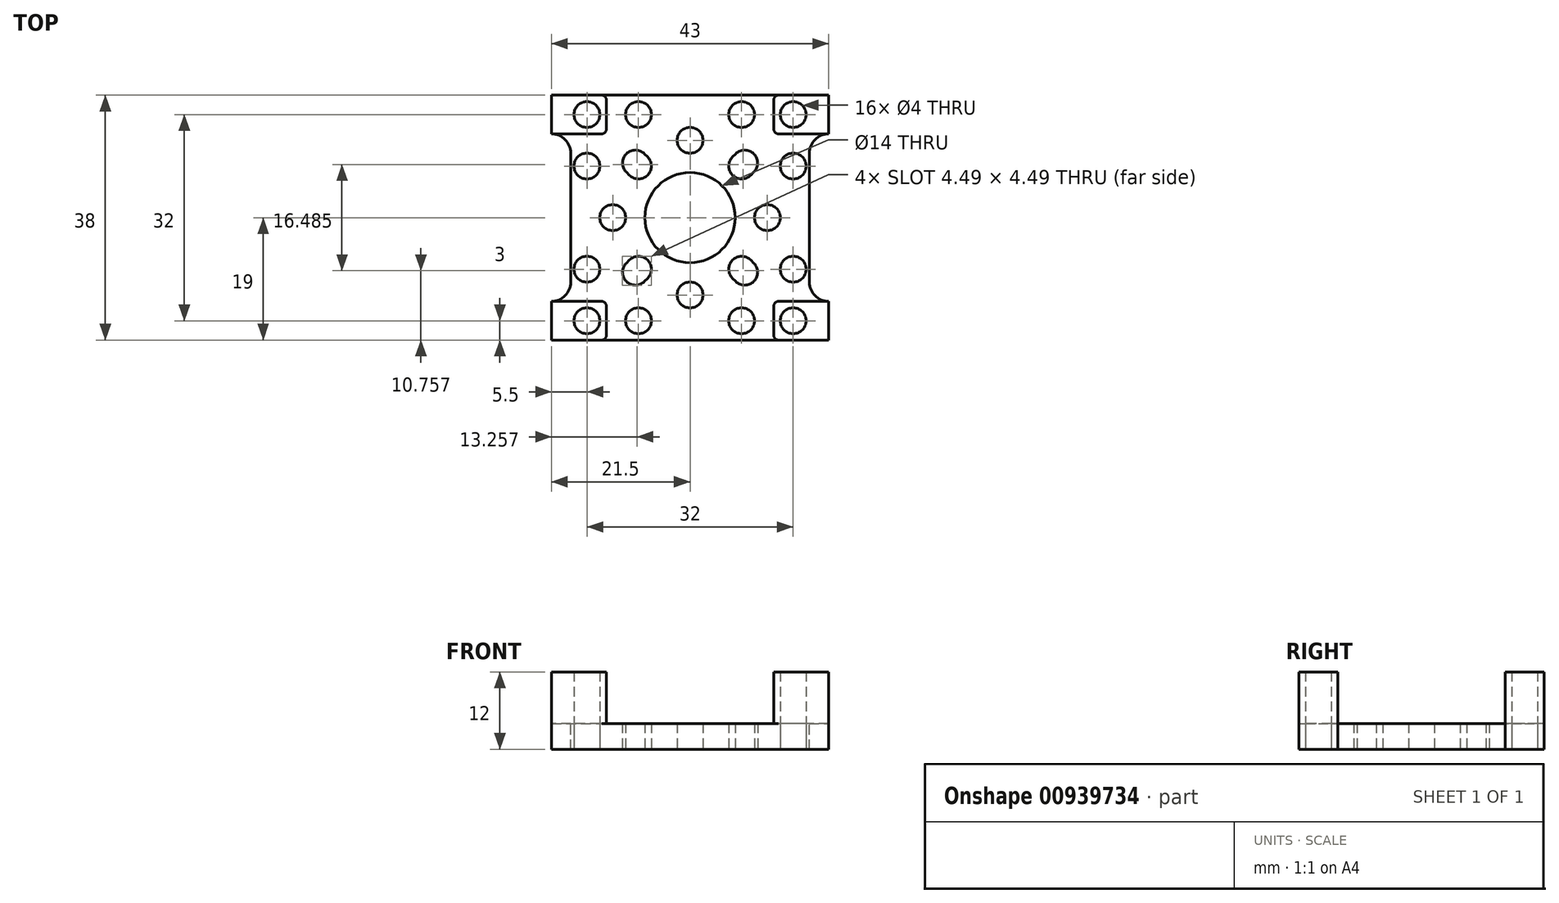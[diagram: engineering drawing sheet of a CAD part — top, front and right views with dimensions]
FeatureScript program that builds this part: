
annotation { "Feature Type Name" : "Feature", "Feature Type Description" : "" }
export const myFeature = defineFeature(function(context is Context, id is Id, definition is map)
    precondition{}
    {
        {
            var Q0;
            Q0=qCreatedBy(makeId("Top.planeOp"),FACE);
            var sketch = newSketch(context, id + "F0", { "sketchPlane" : qUnion([Q0])});
            skCircle(sketch, "E0", {"center": v(0, 0) * mm, "radius": 7 * mm});
            skCircle(sketch, "E1", {"center": v(0, 12) * mm, "radius": 2 * mm});
            skCircle(sketch, "E2", {"center": v(0, -12) * mm, "radius": 2 * mm});
            skCircle(sketch, "E3", {"center": v(12, 0) * mm, "radius": 2 * mm});
            skCircle(sketch, "E4", {"center": v(-12, 0) * mm, "radius": 2 * mm});
            skLineSegment(sketch, "E5", {"start": v(0, 12) * mm, "end": v(0, 0) * mm, "construction": true});
            skLineSegment(sketch, "E6", {"start": v(0, -12) * mm, "end": v(0, 0) * mm, "construction": true});
            skLineSegment(sketch, "E7", {"start": v(12, 0) * mm, "end": v(0, 0) * mm, "construction": true});
            skLineSegment(sketch, "E8", {"start": v(-12, 0) * mm, "end": v(0, 0) * mm, "construction": true});
            skLineSegment(sketch, "E9.bottom", {"start": v(8, 8) * mm, "end": v(-8, 8) * mm, "construction": true});
            skLineSegment(sketch, "E9.top", {"start": v(8, -8) * mm, "end": v(-8, -8) * mm, "construction": true});
            skLineSegment(sketch, "E9.left", {"start": v(8, 8) * mm, "end": v(8, -8) * mm, "construction": true});
            skLineSegment(sketch, "E9.right", {"start": v(-8, 8) * mm, "end": v(-8, -8) * mm, "construction": true});
            skArc(sketch, "E10", {"start": v(6.59, 9.41) * mm, "mid": v(6.59, 6.59) * mm, "end": v(9.41, 6.59) * mm});
            skArc(sketch, "E11", {"start": v(-9.41, 6.59) * mm, "mid": v(-6.59, 6.59) * mm, "end": v(-6.59, 9.41) * mm});
            skArc(sketch, "E12", {"start": v(-6.59, -9.41) * mm, "mid": v(-6.59, -6.59) * mm, "end": v(-9.41, -6.59) * mm});
            skArc(sketch, "E13", {"start": v(9.41, -6.59) * mm, "mid": v(6.59, -6.59) * mm, "end": v(6.59, -9.41) * mm});
            skLineSegment(sketch, "E14", {"start": v(0, 0) * mm, "end": v(-8.49, 8.49) * mm, "construction": true});
            skArc(sketch, "E15", {"start": v(-7.07, 9.9) * mm, "mid": v(-9.9, 9.9) * mm, "end": v(-9.9, 7.07) * mm});
            skLineSegment(sketch, "E16", {"start": v(0, 0) * mm, "end": v(8.49, 8.49) * mm, "construction": true});
            skLineSegment(sketch, "E17", {"start": v(0, 0) * mm, "end": v(8.49, -8.49) * mm, "construction": true});
            skLineSegment(sketch, "E18", {"start": v(0, 0) * mm, "end": v(-8.49, -8.49) * mm, "construction": true});
            skArc(sketch, "E19", {"start": v(7.07, -9.9) * mm, "mid": v(9.9, -9.9) * mm, "end": v(9.9, -7.07) * mm});
            skArc(sketch, "E20", {"start": v(-9.9, -7.07) * mm, "mid": v(-9.9, -9.9) * mm, "end": v(-7.07, -9.9) * mm});
            skLineSegment(sketch, "E21", {"start": v(-6.59, 9.41) * mm, "end": v(-7.07, 9.9) * mm});
            skLineSegment(sketch, "E22", {"start": v(-9.9, 7.07) * mm, "end": v(-9.41, 6.59) * mm});
            skLineSegment(sketch, "E23", {"start": v(9.9, 7.07) * mm, "end": v(9.41, 6.59) * mm});
            skLineSegment(sketch, "E24", {"start": v(7.07, 9.9) * mm, "end": v(6.59, 9.41) * mm});
            skLineSegment(sketch, "E25", {"start": v(9.41, -6.59) * mm, "end": v(9.9, -7.07) * mm});
            skLineSegment(sketch, "E26", {"start": v(6.59, -9.41) * mm, "end": v(7.07, -9.9) * mm});
            skLineSegment(sketch, "E27", {"start": v(-9.41, -6.59) * mm, "end": v(-9.9, -7.07) * mm});
            skLineSegment(sketch, "E28", {"start": v(-6.59, -9.41) * mm, "end": v(-7.07, -9.9) * mm});
            skArc(sketch, "E29.trimOffspring", {"start": v(9.9, 7.07) * mm, "mid": v(9.9, 9.9) * mm, "end": v(7.07, 9.9) * mm});
            skLineSegment(sketch, "E30.bottom", {"start": v(0, 0) * mm, "end": v(16, 0) * mm, "construction": true});
            skLineSegment(sketch, "E30.top", {"start": v(0, 16) * mm, "end": v(16, 16) * mm, "construction": true});
            skLineSegment(sketch, "E30.left", {"start": v(0, 0) * mm, "end": v(0, 16) * mm, "construction": true});
            skLineSegment(sketch, "E30.right", {"start": v(16, 0) * mm, "end": v(16, 16) * mm, "construction": true});
            skCircle(sketch, "E31", {"center": v(16, 16) * mm, "radius": 2 * mm});
            skCircle(sketch, "E32", {"center": v(8, 16) * mm, "radius": 2 * mm});
            skCircle(sketch, "E33", {"center": v(16, 8) * mm, "radius": 2 * mm});
            skPoint(sketch, "E33.perimeterSnap0", {"position": v(16, 8) * mm});
            skCircle(sketch, "E34.1.0", {"center": v(-16, 8) * mm, "radius": 2 * mm});
            skCircle(sketch, "E34.1.1", {"center": v(-16, 16) * mm, "radius": 2 * mm});
            skCircle(sketch, "E34.1.2", {"center": v(-8, 16) * mm, "radius": 2 * mm});
            skCircle(sketch, "E34.2.0", {"center": v(-8, -16) * mm, "radius": 2 * mm});
            skCircle(sketch, "E34.2.1", {"center": v(-16, -16) * mm, "radius": 2 * mm});
            skCircle(sketch, "E34.2.2", {"center": v(-16, -8) * mm, "radius": 2 * mm});
            skCircle(sketch, "E34.3.0", {"center": v(16, -8) * mm, "radius": 2 * mm});
            skCircle(sketch, "E34.3.1", {"center": v(16, -16) * mm, "radius": 2 * mm});
            skCircle(sketch, "E34.3.2", {"center": v(8, -16) * mm, "radius": 2 * mm});
            skLineSegment(sketch, "E35.bottom", {"start": v(21.5, 19) * mm, "end": v(-21.5, 19) * mm});
            skLineSegment(sketch, "E35.top", {"start": v(21.5, -19) * mm, "end": v(-21.5, -19) * mm});
            skLineSegment(sketch, "E35.left", {"start": v(21.5, 19) * mm, "end": v(21.5, -19) * mm});
            skLineSegment(sketch, "E35.right", {"start": v(-21.5, 19) * mm, "end": v(-21.5, -19) * mm});
            skSolve(sketch);
        }
        {
            var Q0;
            Q0=qSketchRegion(id+"F0",true);
            extrude(context, id + "F1", {"entities" : qUnion([Q0]), "depth" : 4 * mm, "offsetDistance" : 25 * mm});
        }
        {
            var Q0;
            Q0=makeQuery(id+"F1.opExtrude","CAP_FACE",FACE,{"disambiguationData":[OSD([sQuery(id+"F0.wireOp",EDGE,"E0"),sQuery(id+"F0.wireOp",EDGE,"E1"),sQuery(id+"F0.wireOp",EDGE,"E2"),sQuery(id+"F0.wireOp",EDGE,"E3"),sQuery(id+"F0.wireOp",EDGE,"E4"),sQuery(id+"F0.wireOp",EDGE,"E10"),sQuery(id+"F0.wireOp",EDGE,"E11"),sQuery(id+"F0.wireOp",EDGE,"E12"),sQuery(id+"F0.wireOp",EDGE,"E13"),sQuery(id+"F0.wireOp",EDGE,"E15"),sQuery(id+"F0.wireOp",EDGE,"E19"),sQuery(id+"F0.wireOp",EDGE,"E20"),sQuery(id+"F0.wireOp",EDGE,"E21"),sQuery(id+"F0.wireOp",EDGE,"E22"),sQuery(id+"F0.wireOp",EDGE,"E23"),sQuery(id+"F0.wireOp",EDGE,"E24"),sQuery(id+"F0.wireOp",EDGE,"E25"),sQuery(id+"F0.wireOp",EDGE,"E26"),sQuery(id+"F0.wireOp",EDGE,"E27"),sQuery(id+"F0.wireOp",EDGE,"E28"),sQuery(id+"F0.wireOp",EDGE,"E29.trimOffspring"),sQuery(id+"F0.wireOp",EDGE,"E31"),sQuery(id+"F0.wireOp",EDGE,"E32"),sQuery(id+"F0.wireOp",EDGE,"E33"),sQuery(id+"F0.wireOp",EDGE,"E34.1.0"),sQuery(id+"F0.wireOp",EDGE,"E34.1.1"),sQuery(id+"F0.wireOp",EDGE,"E34.1.2"),sQuery(id+"F0.wireOp",EDGE,"E34.2.0"),sQuery(id+"F0.wireOp",EDGE,"E34.2.1"),sQuery(id+"F0.wireOp",EDGE,"E34.2.2"),sQuery(id+"F0.wireOp",EDGE,"E34.3.0"),sQuery(id+"F0.wireOp",EDGE,"E34.3.1"),sQuery(id+"F0.wireOp",EDGE,"E34.3.2"),sQuery(id+"F0.wireOp",EDGE,"E35.bottom"),sQuery(id+"F0.wireOp",EDGE,"E35.top"),sQuery(id+"F0.wireOp",EDGE,"E35.left"),sQuery(id+"F0.wireOp",EDGE,"E35.right")])],"isStart":false});
            var sketch = newSketch(context, id + "F2", { "sketchPlane" : qUnion([Q0])});
            skLineSegment(sketch, "E36.0", {"start": v(21.5, 19) * mm, "end": v(-21.5, 19) * mm, "construction": true});
            skLineSegment(sketch, "E37.0", {"start": v(-21.5, 19) * mm, "end": v(-21.5, -19) * mm, "construction": true});
            skLineSegment(sketch, "E38.bottom", {"start": v(-21.5, 19) * mm, "end": v(-13, 19) * mm});
            skLineSegment(sketch, "E38.top", {"start": v(-21.5, 13) * mm, "end": v(-13, 13) * mm});
            skLineSegment(sketch, "E38.left", {"start": v(-21.5, 19) * mm, "end": v(-21.5, 13) * mm});
            skLineSegment(sketch, "E38.right", {"start": v(-13, 19) * mm, "end": v(-13, 13) * mm});
            skLineSegment(sketch, "E39.bottom", {"start": v(21.5, 19) * mm, "end": v(13, 19) * mm});
            skLineSegment(sketch, "E39.top", {"start": v(21.5, 13) * mm, "end": v(13, 13) * mm});
            skLineSegment(sketch, "E39.left", {"start": v(21.5, 19) * mm, "end": v(21.5, 13) * mm});
            skLineSegment(sketch, "E39.right", {"start": v(13, 19) * mm, "end": v(13, 13) * mm});
            skLineSegment(sketch, "E40.1.0", {"start": v(13, -19) * mm, "end": v(13, -13) * mm});
            skLineSegment(sketch, "E40.1.1", {"start": v(-13, -19) * mm, "end": v(-13, -13) * mm});
            skLineSegment(sketch, "E40.1.2", {"start": v(-21.5, -19) * mm, "end": v(21.5, -19) * mm, "construction": true});
            skLineSegment(sketch, "E40.1.3", {"start": v(21.5, -19) * mm, "end": v(21.5, -13) * mm});
            skLineSegment(sketch, "E40.1.4", {"start": v(-21.5, -13) * mm, "end": v(-13, -13) * mm});
            skLineSegment(sketch, "E40.1.5", {"start": v(21.5, -13) * mm, "end": v(13, -13) * mm});
            skLineSegment(sketch, "E40.1.6", {"start": v(-21.5, -19) * mm, "end": v(-21.5, -13) * mm});
            skLineSegment(sketch, "E40.1.7", {"start": v(21.5, -19) * mm, "end": v(13, -19) * mm});
            skLineSegment(sketch, "E40.1.8", {"start": v(-21.5, -19) * mm, "end": v(-13, -19) * mm});
            skPoint(sketch, "E40.center", {"position": v(0, 0) * mm});
            skCircle(sketch, "E41.0", {"center": v(-16, 16) * mm, "radius": 2 * mm});
            skCircle(sketch, "E42.0", {"center": v(16, 16) * mm, "radius": 2 * mm});
            skCircle(sketch, "E43.0", {"center": v(16, -16) * mm, "radius": 2 * mm});
            skCircle(sketch, "E44.0", {"center": v(-16, -16) * mm, "radius": 2 * mm});
            skSolve(sketch);
        }
        {
            var Q0;
            Q0=qSketchRegion(id+"F2",true);
            extrude(context, id + "F3", {"entities" : qUnion([Q0]), "operationType" : NewBodyOperationType.ADD, "depth" : 8 * mm, "offsetDistance" : 25 * mm});
        }
        {
            var Q0;
            Q0=makeQuery(id+"F1.opExtrude","CAP_FACE",FACE,{"disambiguationData":[OSD([sQuery(id+"F0.wireOp",EDGE,"E0"),sQuery(id+"F0.wireOp",EDGE,"E1"),sQuery(id+"F0.wireOp",EDGE,"E2"),sQuery(id+"F0.wireOp",EDGE,"E3"),sQuery(id+"F0.wireOp",EDGE,"E4"),sQuery(id+"F0.wireOp",EDGE,"E10"),sQuery(id+"F0.wireOp",EDGE,"E11"),sQuery(id+"F0.wireOp",EDGE,"E12"),sQuery(id+"F0.wireOp",EDGE,"E13"),sQuery(id+"F0.wireOp",EDGE,"E15"),sQuery(id+"F0.wireOp",EDGE,"E19"),sQuery(id+"F0.wireOp",EDGE,"E20"),sQuery(id+"F0.wireOp",EDGE,"E21"),sQuery(id+"F0.wireOp",EDGE,"E22"),sQuery(id+"F0.wireOp",EDGE,"E23"),sQuery(id+"F0.wireOp",EDGE,"E24"),sQuery(id+"F0.wireOp",EDGE,"E25"),sQuery(id+"F0.wireOp",EDGE,"E26"),sQuery(id+"F0.wireOp",EDGE,"E27"),sQuery(id+"F0.wireOp",EDGE,"E28"),sQuery(id+"F0.wireOp",EDGE,"E29.trimOffspring"),sQuery(id+"F0.wireOp",EDGE,"E31"),sQuery(id+"F0.wireOp",EDGE,"E32"),sQuery(id+"F0.wireOp",EDGE,"E33"),sQuery(id+"F0.wireOp",EDGE,"E34.1.0"),sQuery(id+"F0.wireOp",EDGE,"E34.1.1"),sQuery(id+"F0.wireOp",EDGE,"E34.1.2"),sQuery(id+"F0.wireOp",EDGE,"E34.2.0"),sQuery(id+"F0.wireOp",EDGE,"E34.2.1"),sQuery(id+"F0.wireOp",EDGE,"E34.2.2"),sQuery(id+"F0.wireOp",EDGE,"E34.3.0"),sQuery(id+"F0.wireOp",EDGE,"E34.3.1"),sQuery(id+"F0.wireOp",EDGE,"E34.3.2"),sQuery(id+"F0.wireOp",EDGE,"E35.bottom"),sQuery(id+"F0.wireOp",EDGE,"E35.top"),sQuery(id+"F0.wireOp",EDGE,"E35.left"),sQuery(id+"F0.wireOp",EDGE,"E35.right")])],"isStart":false});
            var sketch = newSketch(context, id + "F4", { "sketchPlane" : qUnion([Q0])});
            skPoint(sketch, "E45.0", {"position": v(-21.5, 13) * mm});
            skPoint(sketch, "E46.0", {"position": v(-21.5, -13) * mm});
            skLineSegment(sketch, "E47.bottom", {"start": v(-21.5, 13) * mm, "end": v(-18.5, 13) * mm});
            skLineSegment(sketch, "E47.top", {"start": v(-21.5, -13) * mm, "end": v(-18.5, -13) * mm});
            skLineSegment(sketch, "E47.left", {"start": v(-21.5, 13) * mm, "end": v(-21.5, -13) * mm});
            skLineSegment(sketch, "E47.right", {"start": v(-18.5, 13) * mm, "end": v(-18.5, -13) * mm});
            skLineSegment(sketch, "E48.1.0", {"start": v(21.5, 13) * mm, "end": v(18.5, 13) * mm});
            skLineSegment(sketch, "E48.1.1", {"start": v(21.5, -13) * mm, "end": v(18.5, -13) * mm});
            skLineSegment(sketch, "E48.1.2", {"start": v(18.5, -13) * mm, "end": v(18.5, 13) * mm});
            skPoint(sketch, "E48.1.3", {"position": v(21.5, 13) * mm});
            skLineSegment(sketch, "E48.1.4", {"start": v(21.5, -13) * mm, "end": v(21.5, 13) * mm});
            skPoint(sketch, "E48.1.5", {"position": v(21.5, -13) * mm});
            skPoint(sketch, "E48.center", {"position": v(0, 0) * mm});
            skSolve(sketch);
        }
        {
            var Q0;
            Q0=qSketchRegion(id+"F4",true);
            extrude(context, id + "F5", {"entities" : qUnion([Q0]), "operationType" : NewBodyOperationType.REMOVE, "oppositeDirection" : true, "depth" : 25 * mm, "offsetDistance" : 25 * mm});
        }
        {
            var Q0;
            Q0=makeQuery(id+"F5.boolean.opBoolean","COPY",EDGE,{"derivedFrom":makeQuery(id+"F5.opExtrude","SWEPT_EDGE",EDGE,{"disambiguationData":[OSD([sQuery(id+"F2.wireOp",EDGE,"E38.top"),sQuery(id+"F4.wireOp",EDGE,"E47.bottom"),sQuery(id+"F4.wireOp",EDGE,"E47.right")])]})});
            var Q1;
            Q1=makeQuery(id+"F5.boolean.opBoolean","COPY",EDGE,{"derivedFrom":makeQuery(id+"F5.opExtrude","SWEPT_EDGE",EDGE,{"disambiguationData":[OSD([sQuery(id+"F2.wireOp",EDGE,"E40.1.4"),sQuery(id+"F4.wireOp",EDGE,"E47.top"),sQuery(id+"F4.wireOp",EDGE,"E47.right")])]})});
            var Q2;
            Q2=makeQuery(id+"F5.boolean.opBoolean","COPY",EDGE,{"derivedFrom":makeQuery(id+"F5.opExtrude","SWEPT_EDGE",EDGE,{"disambiguationData":[OSD([sQuery(id+"F2.wireOp",EDGE,"E39.top"),sQuery(id+"F4.wireOp",EDGE,"E48.1.0"),sQuery(id+"F4.wireOp",EDGE,"E48.1.2")])]})});
            var Q3;
            Q3=makeQuery(id+"F5.boolean.opBoolean","COPY",EDGE,{"derivedFrom":makeQuery(id+"F5.opExtrude","SWEPT_EDGE",EDGE,{"disambiguationData":[OSD([sQuery(id+"F2.wireOp",EDGE,"E40.1.5"),sQuery(id+"F4.wireOp",EDGE,"E48.1.1"),sQuery(id+"F4.wireOp",EDGE,"E48.1.2")])]})});
            fillet(context, id + "F6", {"entities" : qUnion([Q0, Q1, Q2, Q3]), "radius" : 3 * mm, "tangentPropagation" : true, "allowEdgeOverflow" : false});
        }
        {
            var Q0;
            Q0=makeQuery(id+"F3.opExtrude","SWEPT_EDGE",EDGE,{"disambiguationData":[OSD([sQuery(id+"F2.wireOp",EDGE,"E39.top"),sQuery(id+"F2.wireOp",EDGE,"E39.right")])]});
            var Q1;
            Q1=makeQuery(id+"F3.opExtrude","SWEPT_EDGE",EDGE,{"disambiguationData":[OSD([sQuery(id+"F0.wireOp",EDGE,"E35.top"),sQuery(id+"F2.wireOp",EDGE,"E40.1.0"),sQuery(id+"F2.wireOp",EDGE,"E40.1.7")])]});
            var Q2;
            Q2=makeQuery(id+"F3.opExtrude","SWEPT_EDGE",EDGE,{"disambiguationData":[OSD([sQuery(id+"F2.wireOp",EDGE,"E40.1.0"),sQuery(id+"F2.wireOp",EDGE,"E40.1.5")])]});
            var Q3;
            Q3=makeQuery(id+"F3.opExtrude","SWEPT_EDGE",EDGE,{"disambiguationData":[OSD([sQuery(id+"F0.wireOp",EDGE,"E35.top"),sQuery(id+"F2.wireOp",EDGE,"E40.1.1"),sQuery(id+"F2.wireOp",EDGE,"E40.1.8")])]});
            var Q4;
            Q4=makeQuery(id+"F3.opExtrude","SWEPT_EDGE",EDGE,{"disambiguationData":[OSD([sQuery(id+"F2.wireOp",EDGE,"E38.top"),sQuery(id+"F2.wireOp",EDGE,"E38.right")])]});
            var Q5;
            Q5=makeQuery(id+"F3.opExtrude","SWEPT_EDGE",EDGE,{"disambiguationData":[OSD([sQuery(id+"F0.wireOp",EDGE,"E35.bottom"),sQuery(id+"F2.wireOp",EDGE,"E38.bottom"),sQuery(id+"F2.wireOp",EDGE,"E38.right")])]});
            var Q6;
            Q6=makeQuery(id+"F3.opExtrude","SWEPT_EDGE",EDGE,{"disambiguationData":[OSD([sQuery(id+"F2.wireOp",EDGE,"E40.1.1"),sQuery(id+"F2.wireOp",EDGE,"E40.1.4")])]});
            var Q7;
            Q7=makeQuery(id+"F3.opExtrude","SWEPT_EDGE",EDGE,{"disambiguationData":[OSD([sQuery(id+"F0.wireOp",EDGE,"E35.bottom"),sQuery(id+"F2.wireOp",EDGE,"E39.bottom"),sQuery(id+"F2.wireOp",EDGE,"E39.right")])]});
            fillet(context, id + "F7", {"entities" : qUnion([Q0, Q1, Q2, Q3, Q4, Q5, Q6, Q7]), "radius" : 0.7 * mm, "tangentPropagation" : true, "allowEdgeOverflow" : false});
        }
    });
